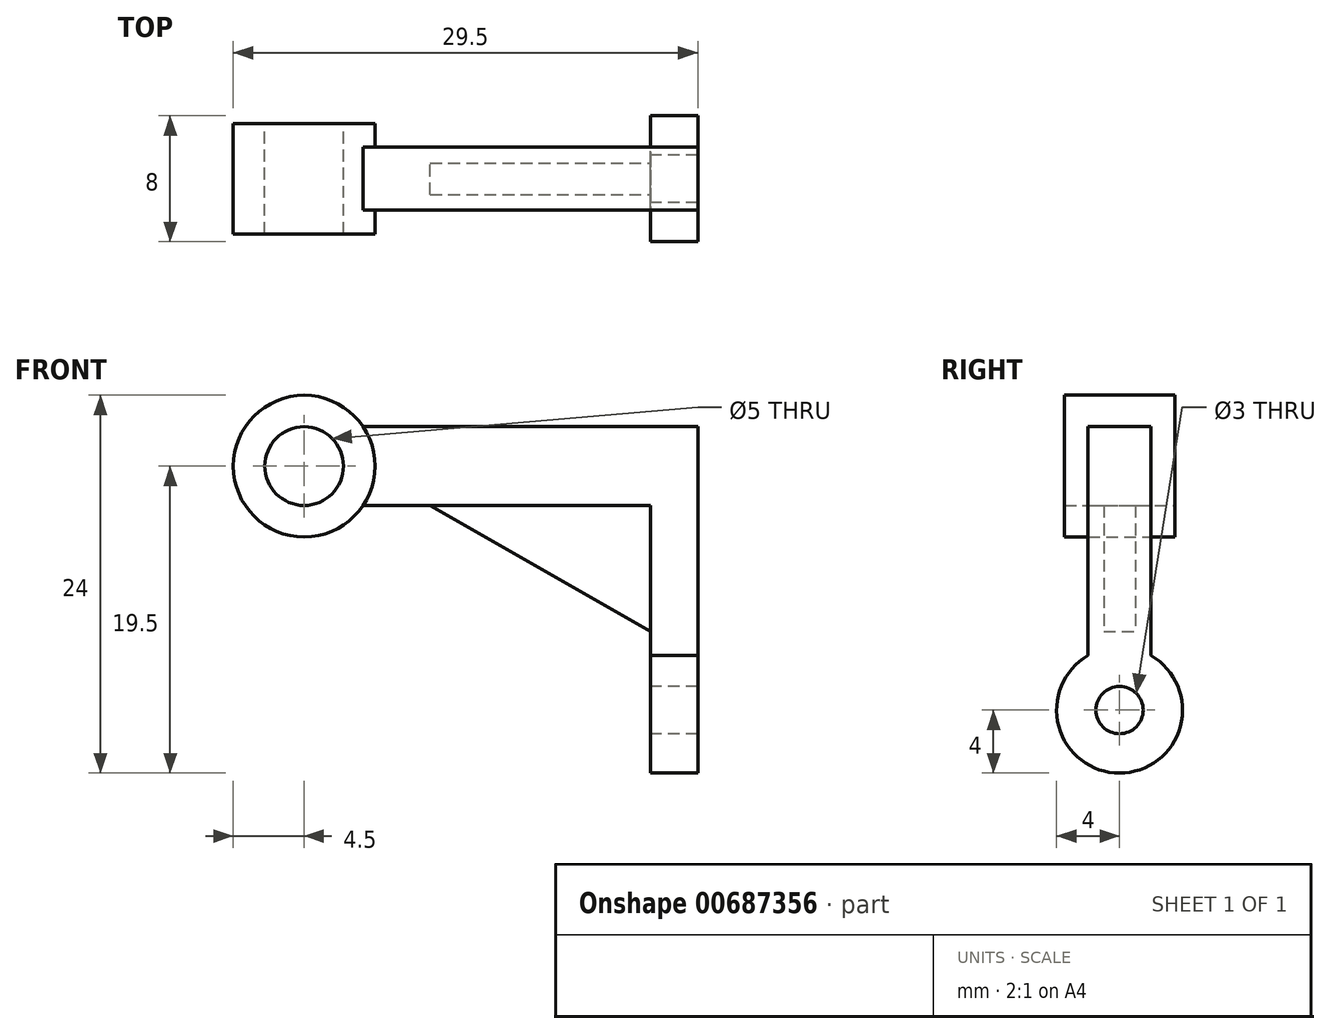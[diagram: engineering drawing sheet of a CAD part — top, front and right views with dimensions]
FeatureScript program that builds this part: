
annotation { "Feature Type Name" : "Feature", "Feature Type Description" : "" }
export const myFeature = defineFeature(function(context is Context, id is Id, definition is map)
    precondition{}
    {
        {
            var Q0;
            Q0=qCreatedBy(makeId("Front.planeOp"),FACE);
            var sketch = newSketch(context, id + "F0", { "sketchPlane" : qUnion([Q0])});
            skLineSegment(sketch, "E0", {"start": v(-16.69, 5) * mm, "end": v(5.31, 5) * mm});
            skLineSegment(sketch, "E1", {"start": v(5.31, 5) * mm, "end": v(5.31, -15) * mm});
            skLineSegment(sketch, "E2", {"start": v(5.31, -15) * mm, "end": v(2.31, -15) * mm});
            skLineSegment(sketch, "E3", {"start": v(2.31, -15) * mm, "end": v(2.31, 0) * mm});
            skLineSegment(sketch, "E4", {"start": v(2.31, 0) * mm, "end": v(-16.69, 0) * mm});
            skLineSegment(sketch, "E5", {"start": v(-16.69, 0) * mm, "end": v(-16.69, 5) * mm});
            skCircle(sketch, "E6", {"center": v(-19.69, 2.5) * mm, "radius": 4.5 * mm});
            skPoint(sketch, "E6.centerSnap0", {"position": v(-16.69, 2.5) * mm});
            skCircle(sketch, "E7", {"center": v(-19.69, 2.5) * mm, "radius": 2.5 * mm});
            skSolve(sketch);
        }
        {
            var Q0;
            {var subQ0=sQuery(id+"F0.wireOp",EDGE,"E5");Q0=makeQuery(id+"F0.imprint","IMPRINT",FACE,{"disambiguationData":[TD([[makeQuery(id+"F0.imprint","IMPRINT",EDGE,{"derivedFrom":subQ0}),-1.0]])]});}
            var Q1;
            {var subQ5=sQuery(id+"F0.wireOp",EDGE,"E5");Q1=makeQuery(id+"F0.imprint","IMPRINT",FACE,{"disambiguationData":[TD([[makeQuery(id+"F0.imprint","IMPRINT",EDGE,{"derivedFrom":subQ5}),1.0]])]});}
            extrude(context, id + "F1", {"entities" : qUnion([Q0, Q1]), "endBound" : BoundingType.SYMMETRIC, "depth" : 7 * mm, "offsetDistance" : 25 * mm});
        }
        {
            var Q0;
            Q0 = qSketchRegion(id + "F0", true);
            extrude(context, id + "F2", {"entities" : qUnion([Q0]), "operationType" : NewBodyOperationType.ADD, "endBound" : BoundingType.SYMMETRIC, "depth" : 4 * mm, "offsetDistance" : 25 * mm});
        }
        {
            var Q0;
            Q0=makeQuery(id+"F2.opExtrude","SWEPT_FACE",FACE,{"disambiguationData":[OSD([sQuery(id+"F0.wireOp",EDGE,"E3")])]});
            var sketch = newSketch(context, id + "F3", { "sketchPlane" : qUnion([Q0])});
            skCircle(sketch, "E8", {"center": v(0, -13) * mm, "radius": 4 * mm});
            skSolve(sketch);
        }
        {
            var Q0;
            {var subQ1=sQuery(id+"F0.wireOp",EDGE,"E3");var subQ6=makeQuery(id+"F2.opExtrude","SWEPT_EDGE",EDGE,{"disambiguationData":[OSD([sQuery(id+"F0.wireOp",EDGE,"E2"),subQ1])]});Q0=makeQuery(id+"F3.imprint","IMPRINT",FACE,{"disambiguationData":[TD([[makeQuery(id+"F3.imprint","IMPRINT",EDGE,{"derivedFrom":subQ6}),1.0]])]});}
            extrude(context, id + "F4", {"entities" : qUnion([Q0]), "operationType" : NewBodyOperationType.ADD, "oppositeDirection" : true, "depth" : 3 * mm, "offsetDistance" : 25 * mm});
        }
        {
            var Q0;
            {var subQ0=sQuery(id+"F0.wireOp",EDGE,"E3");Q0=makeQuery(id+"F4.boolean.opBoolean","MERGE",FACE,{"derivedFrom":[makeQuery(id+"F2.opExtrude","SWEPT_FACE",FACE,{"disambiguationData":[OSD([subQ0])]}),makeQuery(id+"F4.opExtrude","CAP_FACE",FACE,{"disambiguationData":[OSD([sQuery(id+"F0.wireOp",EDGE,"E2"),subQ0,sQuery(id+"F3.wireOp",EDGE,"E8")])],"isStart":true})]});}
            var sketch = newSketch(context, id + "F5", { "sketchPlane" : qUnion([Q0])});
            skCircle(sketch, "E9", {"center": v(0, -13) * mm, "radius": 1.5 * mm});
            skSolve(sketch);
        }
        {
            var Q0;
            Q0=sQuery(id+"F5.wireOp",VERTEX,"E9.center");
            var Q1;
            Q1=makeQuery(id+"F1.opExtrude","SWEPT_BODY",BODY,{"disambiguationData":[OSD([sQuery(id+"F0.wireOp",EDGE,"E6"),sQuery(id+"F0.wireOp",EDGE,"E7")])]});
            hole(context, id + "F6", {"style" : HoleStyle.SIMPLE, "endStyle" : HoleEndStyle.THROUGH, "holeDiameter" : 3 * mm, "majorDiameter" : 5 * mm, "isTappedThrough" : true, "tappedDepth" : 12 * mm, "tapClearance" : 3, "startFromSketch" : true, "locations" : qUnion([Q0]), "scope" : qUnion([Q1])});
        }
        {
            var Q0;
            Q0=qCreatedBy(makeId("Front.planeOp"),FACE);
            var sketch = newSketch(context, id + "F7", { "sketchPlane" : qUnion([Q0])});
            skLineSegment(sketch, "E10", {"start": v(-11.69, 0) * mm, "end": v(2.31, 0) * mm});
            skLineSegment(sketch, "E11", {"start": v(2.31, 0) * mm, "end": v(2.31, -8) * mm});
            skLineSegment(sketch, "E12", {"start": v(2.31, -8) * mm, "end": v(-11.69, 0) * mm});
            skSolve(sketch);
        }
        {
            var Q0;
            Q0 = qSketchRegion(id + "F7", true);
            extrude(context, id + "F8", {"entities" : qUnion([Q0]), "operationType" : NewBodyOperationType.ADD, "endBound" : BoundingType.SYMMETRIC, "depth" : 2 * mm, "offsetDistance" : 25 * mm});
        }
    });
